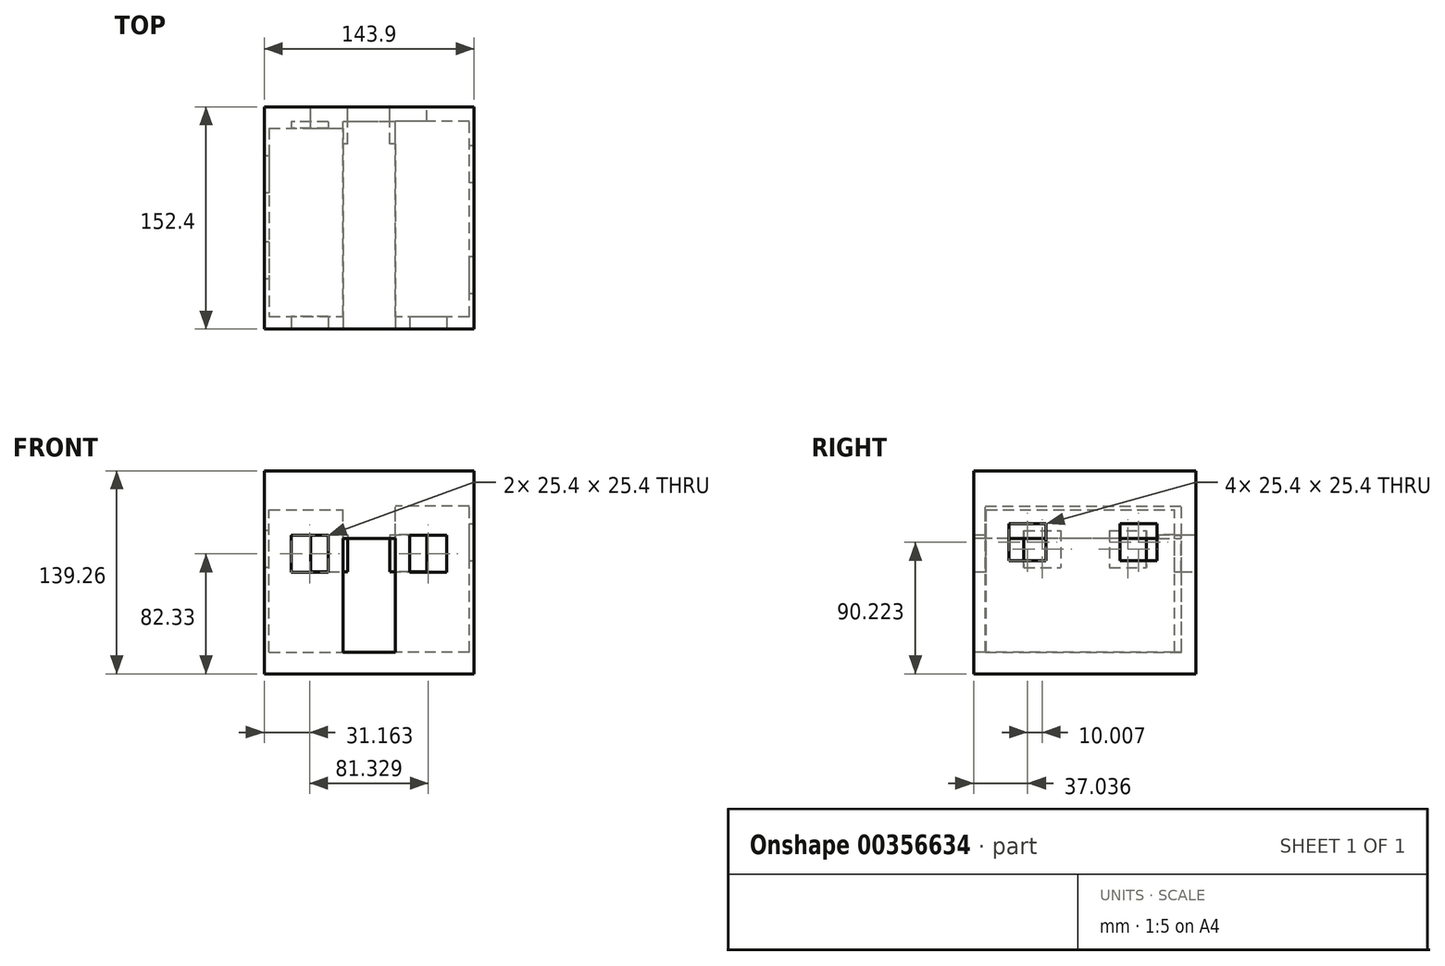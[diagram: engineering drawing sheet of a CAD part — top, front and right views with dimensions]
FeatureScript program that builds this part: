
annotation { "Feature Type Name" : "Feature", "Feature Type Description" : "" }
export const myFeature = defineFeature(function(context is Context, id is Id, definition is map)
    precondition{}
    {
        {
            var Q0;
            Q0=qCreatedBy(makeId("Front.planeOp"),FACE);
            var sketch = newSketch(context, id + "F0", { "sketchPlane" : qUnion([Q0])});
            skLineSegment(sketch, "E0.bottom", {"start": v(71.95, 69.63) * mm, "end": v(-71.95, 69.63) * mm});
            skLineSegment(sketch, "E0.top", {"start": v(71.95, -69.63) * mm, "end": v(-71.95, -69.63) * mm});
            skLineSegment(sketch, "E0.left", {"start": v(71.95, 69.63) * mm, "end": v(71.95, -69.63) * mm});
            skLineSegment(sketch, "E0.right", {"start": v(-71.95, 69.63) * mm, "end": v(-71.95, -69.63) * mm});
            skPoint(sketch, "E0.middle", {"position": v(0, 0) * mm});
            skSolve(sketch);
        }
        {
            var Q0;
            Q0=makeQuery(id+"F0.imprint","IMPRINT",FACE,{"disambiguationData":[TD([[makeQuery(id+"F0.imprint","IMPRINT",EDGE,{"derivedFrom":sQuery(id+"F0.wireOp",EDGE,"E0.bottom")}),1.0]])]});
            extrude(context, id + "F1", {"entities" : qUnion([Q0]), "depth" : 152.4 * mm});
        }
        {
            var Q0;
            Q0=makeQuery(id+"F1.opExtrude","CAP_FACE",FACE,{"disambiguationData":[OSD([sQuery(id+"F0.wireOp",EDGE,"E0.bottom"),sQuery(id+"F0.wireOp",EDGE,"E0.top"),sQuery(id+"F0.wireOp",EDGE,"E0.left"),sQuery(id+"F0.wireOp",EDGE,"E0.right")])],"isStart":false});
            var sketch = newSketch(context, id + "F2", { "sketchPlane" : qUnion([Q0])});
            skLineSegment(sketch, "E1.bottom", {"start": v(17.83, 23.45) * mm, "end": v(-17.83, 23.45) * mm});
            skLineSegment(sketch, "E1.top", {"start": v(17.83, -54.7) * mm, "end": v(-17.83, -54.7) * mm});
            skLineSegment(sketch, "E1.left", {"start": v(17.83, 23.45) * mm, "end": v(17.83, -54.7) * mm});
            skLineSegment(sketch, "E1.right", {"start": v(-17.83, 23.45) * mm, "end": v(-17.83, -54.7) * mm});
            skPoint(sketch, "E1.middle", {"position": v(0, -15.63) * mm});
            skLineSegment(sketch, "E2.bottom", {"start": v(-28.09, 0) * mm, "end": v(-53.49, 0) * mm});
            skLineSegment(sketch, "E2.top", {"start": v(-28.09, 25.4) * mm, "end": v(-53.49, 25.4) * mm});
            skLineSegment(sketch, "E2.left", {"start": v(-28.09, 0) * mm, "end": v(-28.09, 25.4) * mm});
            skLineSegment(sketch, "E2.right", {"start": v(-53.49, 0) * mm, "end": v(-53.49, 25.4) * mm});
            skPoint(sketch, "E2.middle", {"position": v(-40.79, 12.7) * mm});
            skLineSegment(sketch, "E3.bottom", {"start": v(27.84, 0) * mm, "end": v(53.24, 0) * mm});
            skLineSegment(sketch, "E3.top", {"start": v(27.84, 25.4) * mm, "end": v(53.24, 25.4) * mm});
            skLineSegment(sketch, "E3.left", {"start": v(27.84, 0) * mm, "end": v(27.84, 25.4) * mm});
            skLineSegment(sketch, "E3.right", {"start": v(53.24, 0) * mm, "end": v(53.24, 25.4) * mm});
            skPoint(sketch, "E3.middle", {"position": v(40.54, 12.7) * mm});
            skSolve(sketch);
        }
        {
            var Q0;
            Q0=makeQuery(id+"F2.imprint","IMPRINT",FACE,{"disambiguationData":[TD([[makeQuery(id+"F2.imprint","IMPRINT",EDGE,{"derivedFrom":sQuery(id+"F2.wireOp",EDGE,"E2.bottom")}),-1.0]])]});
            var Q1;
            Q1=makeQuery(id+"F2.imprint","IMPRINT",FACE,{"disambiguationData":[TD([[makeQuery(id+"F2.imprint","IMPRINT",EDGE,{"derivedFrom":sQuery(id+"F2.wireOp",EDGE,"E3.bottom")}),1.0]])]});
            var Q2;
            Q2=makeQuery(id+"F2.imprint","IMPRINT",FACE,{"disambiguationData":[TD([[makeQuery(id+"F2.imprint","IMPRINT",EDGE,{"derivedFrom":sQuery(id+"F2.wireOp",EDGE,"E1.bottom")}),1.0]])]});
            extrude(context, id + "F3", {"entities" : qUnion([Q0, Q1, Q2]), "operationType" : NewBodyOperationType.REMOVE, "oppositeDirection" : true, "depth" : 142.24 * mm});
        }
        {
            var Q0;
            Q0=makeQuery(id+"F3.boolean.opBoolean","COPY",FACE,{"derivedFrom":makeQuery(id+"F3.opExtrude","SWEPT_FACE",FACE,{"disambiguationData":[OSD([sQuery(id+"F2.wireOp",EDGE,"E1.right")])]})});
            var sketch = newSketch(context, id + "F4", { "sketchPlane" : qUnion([Q0])});
            skLineSegment(sketch, "E4.bottom", {"start": v(-143.72, -46.42) * mm, "end": v(-14.63, -46.42) * mm});
            skLineSegment(sketch, "E4.top", {"start": v(-143.72, 42.99) * mm, "end": v(-14.63, 42.99) * mm});
            skLineSegment(sketch, "E4.left", {"start": v(-143.72, -46.42) * mm, "end": v(-143.72, 42.99) * mm});
            skLineSegment(sketch, "E4.right", {"start": v(-14.63, -46.42) * mm, "end": v(-14.63, 42.99) * mm});
            skSolve(sketch);
        }
        {
            var Q0;
            Q0 = qSketchRegion(id + "F4", true);
            extrude(context, id + "F5", {"entities" : qUnion([Q0]), "operationType" : NewBodyOperationType.REMOVE, "oppositeDirection" : true, "depth" : 50.8 * mm});
        }
        {
            var Q0;
            Q0=makeQuery(id+"F3.boolean.opBoolean","COPY",FACE,{"derivedFrom":makeQuery(id+"F3.opExtrude","SWEPT_FACE",FACE,{"disambiguationData":[OSD([sQuery(id+"F2.wireOp",EDGE,"E1.left")])]})});
            var sketch = newSketch(context, id + "F6", { "sketchPlane" : qUnion([Q0])});
            skLineSegment(sketch, "E5.bottom", {"start": v(144.24, -54.7) * mm, "end": v(9.85, -54.7) * mm});
            skLineSegment(sketch, "E5.top", {"start": v(144.24, 45.49) * mm, "end": v(9.85, 45.49) * mm});
            skLineSegment(sketch, "E5.left", {"start": v(144.24, -54.7) * mm, "end": v(144.24, 45.49) * mm});
            skLineSegment(sketch, "E5.right", {"start": v(9.85, -54.7) * mm, "end": v(9.85, 45.49) * mm});
            skSolve(sketch);
        }
        {
            var Q0;
            Q0 = qSketchRegion(id + "F6", true);
            extrude(context, id + "F7", {"entities" : qUnion([Q0]), "operationType" : NewBodyOperationType.REMOVE, "oppositeDirection" : true, "depth" : 50.8 * mm});
        }
        {
            var Q0;
            Q0=makeQuery(id+"F3.boolean.opBoolean","COPY",FACE,{"derivedFrom":makeQuery(id+"F3.opExtrude","SWEPT_FACE",FACE,{"disambiguationData":[OSD([sQuery(id+"F2.wireOp",EDGE,"E1.right")])]})});
            var sketch = newSketch(context, id + "F8", { "sketchPlane" : qUnion([Q0])});
            skLineSegment(sketch, "E6.bottom", {"start": v(-143.72, -46.42) * mm, "end": v(-14.63, -46.42) * mm});
            skLineSegment(sketch, "E6.top", {"start": v(-143.72, -54.7) * mm, "end": v(-14.63, -54.7) * mm});
            skLineSegment(sketch, "E6.left", {"start": v(-143.72, -46.42) * mm, "end": v(-143.72, -54.7) * mm});
            skLineSegment(sketch, "E6.right", {"start": v(-14.63, -46.42) * mm, "end": v(-14.63, -54.7) * mm});
            skSolve(sketch);
        }
        {
            var Q0;
            Q0 = qSketchRegion(id + "F8", true);
            extrude(context, id + "F9", {"entities" : qUnion([Q0]), "operationType" : NewBodyOperationType.REMOVE, "oppositeDirection" : true, "depth" : 50.8 * mm});
        }
        {
            var Q0;
            Q0=makeQuery(id+"F1.opExtrude","SWEPT_FACE",FACE,{"disambiguationData":[OSD([sQuery(id+"F0.wireOp",EDGE,"E0.left")])]});
            var sketch = newSketch(context, id + "F10", { "sketchPlane" : qUnion([Q0])});
            skLineSegment(sketch, "E7.bottom", {"start": v(-102.66, 33.3) * mm, "end": v(-128.06, 33.3) * mm});
            skLineSegment(sketch, "E7.top", {"start": v(-102.66, 7.9) * mm, "end": v(-128.06, 7.9) * mm});
            skLineSegment(sketch, "E7.left", {"start": v(-102.66, 33.3) * mm, "end": v(-102.66, 7.9) * mm});
            skLineSegment(sketch, "E7.right", {"start": v(-128.06, 33.3) * mm, "end": v(-128.06, 7.9) * mm});
            skPoint(sketch, "E7.middle", {"position": v(-115.36, 20.6) * mm});
            skLineSegment(sketch, "E8.bottom", {"start": v(-26.46, 33.3) * mm, "end": v(-51.86, 33.3) * mm});
            skLineSegment(sketch, "E8.top", {"start": v(-26.46, 7.9) * mm, "end": v(-51.86, 7.9) * mm});
            skLineSegment(sketch, "E8.left", {"start": v(-26.46, 33.3) * mm, "end": v(-26.46, 7.9) * mm});
            skLineSegment(sketch, "E8.right", {"start": v(-51.86, 33.3) * mm, "end": v(-51.86, 7.9) * mm});
            skPoint(sketch, "E8.middle", {"position": v(-39.16, 20.6) * mm});
            skSolve(sketch);
        }
        {
            var Q0;
            Q0=makeQuery(id+"F10.imprint","IMPRINT",FACE,{"disambiguationData":[TD([[makeQuery(id+"F10.imprint","IMPRINT",EDGE,{"derivedFrom":sQuery(id+"F10.wireOp",EDGE,"E7.bottom")}),1.0]])]});
            var Q1;
            Q1=makeQuery(id+"F10.imprint","IMPRINT",FACE,{"disambiguationData":[TD([[makeQuery(id+"F10.imprint","IMPRINT",EDGE,{"derivedFrom":sQuery(id+"F10.wireOp",EDGE,"E8.bottom")}),1.0]])]});
            extrude(context, id + "F11", {"entities" : qUnion([Q0, Q1]), "operationType" : NewBodyOperationType.REMOVE, "oppositeDirection" : true, "depth" : 25.4 * mm});
        }
        {
            var Q0;
            Q0=makeQuery(id+"F1.opExtrude","SWEPT_FACE",FACE,{"disambiguationData":[OSD([sQuery(id+"F0.wireOp",EDGE,"E0.right")])]});
            var sketch = newSketch(context, id + "F12", { "sketchPlane" : qUnion([Q0])});
            skLineSegment(sketch, "E9.bottom", {"start": v(59.18, 28.78) * mm, "end": v(33.78, 28.78) * mm});
            skLineSegment(sketch, "E9.top", {"start": v(59.18, 3.38) * mm, "end": v(33.78, 3.38) * mm});
            skLineSegment(sketch, "E9.left", {"start": v(59.18, 28.78) * mm, "end": v(59.18, 3.38) * mm});
            skLineSegment(sketch, "E9.right", {"start": v(33.78, 28.78) * mm, "end": v(33.78, 3.38) * mm});
            skPoint(sketch, "E9.middle", {"position": v(46.48, 16.08) * mm});
            skLineSegment(sketch, "E10.bottom", {"start": v(118.06, 28.78) * mm, "end": v(92.66, 28.78) * mm});
            skLineSegment(sketch, "E10.top", {"start": v(118.06, 3.38) * mm, "end": v(92.66, 3.38) * mm});
            skLineSegment(sketch, "E10.left", {"start": v(118.06, 28.78) * mm, "end": v(118.06, 3.38) * mm});
            skLineSegment(sketch, "E10.right", {"start": v(92.66, 28.78) * mm, "end": v(92.66, 3.38) * mm});
            skPoint(sketch, "E10.middle", {"position": v(105.36, 16.08) * mm});
            skSolve(sketch);
        }
        {
            var Q0;
            Q0=makeQuery(id+"F12.imprint","IMPRINT",FACE,{"disambiguationData":[TD([[makeQuery(id+"F12.imprint","IMPRINT",EDGE,{"derivedFrom":sQuery(id+"F12.wireOp",EDGE,"E9.bottom")}),1.0]])]});
            var Q1;
            Q1=makeQuery(id+"F12.imprint","IMPRINT",FACE,{"disambiguationData":[TD([[makeQuery(id+"F12.imprint","IMPRINT",EDGE,{"derivedFrom":sQuery(id+"F12.wireOp",EDGE,"E10.bottom")}),1.0]])]});
            extrude(context, id + "F13", {"entities" : qUnion([Q0, Q1]), "operationType" : NewBodyOperationType.REMOVE, "oppositeDirection" : true, "depth" : 50.8 * mm});
        }
        {
            var Q0;
            Q0=makeQuery(id+"F1.opExtrude","CAP_FACE",FACE,{"disambiguationData":[OSD([sQuery(id+"F0.wireOp",EDGE,"E0.bottom"),sQuery(id+"F0.wireOp",EDGE,"E0.top"),sQuery(id+"F0.wireOp",EDGE,"E0.left"),sQuery(id+"F0.wireOp",EDGE,"E0.right")])],"isStart":true});
            var sketch = newSketch(context, id + "F14", { "sketchPlane" : qUnion([Q0])});
            skLineSegment(sketch, "E11.bottom", {"start": v(-14.2, 25.9) * mm, "end": v(-39.6, 25.9) * mm});
            skLineSegment(sketch, "E11.top", {"start": v(-14.2, 0.5) * mm, "end": v(-39.6, 0.5) * mm});
            skLineSegment(sketch, "E11.left", {"start": v(-14.2, 25.9) * mm, "end": v(-14.2, 0.5) * mm});
            skLineSegment(sketch, "E11.right", {"start": v(-39.6, 25.9) * mm, "end": v(-39.6, 0.5) * mm});
            skPoint(sketch, "E11.middle", {"position": v(-26.9, 13.2) * mm});
            skLineSegment(sketch, "E12.bottom", {"start": v(40.08, 25.9) * mm, "end": v(14.68, 25.9) * mm});
            skLineSegment(sketch, "E12.top", {"start": v(40.08, 0.5) * mm, "end": v(14.68, 0.5) * mm});
            skLineSegment(sketch, "E12.left", {"start": v(40.08, 25.9) * mm, "end": v(40.08, 0.5) * mm});
            skLineSegment(sketch, "E12.right", {"start": v(14.68, 25.9) * mm, "end": v(14.68, 0.5) * mm});
            skPoint(sketch, "E12.middle", {"position": v(27.38, 13.2) * mm});
            skSolve(sketch);
        }
        {
            var Q0;
            Q0=makeQuery(id+"F14.imprint","IMPRINT",FACE,{"disambiguationData":[TD([[makeQuery(id+"F14.imprint","IMPRINT",EDGE,{"derivedFrom":sQuery(id+"F14.wireOp",EDGE,"E11.bottom")}),1.0]])]});
            var Q1;
            Q1=makeQuery(id+"F14.imprint","IMPRINT",FACE,{"disambiguationData":[TD([[makeQuery(id+"F14.imprint","IMPRINT",EDGE,{"derivedFrom":sQuery(id+"F14.wireOp",EDGE,"E12.bottom")}),1.0]])]});
            extrude(context, id + "F15", {"entities" : qUnion([Q0, Q1]), "operationType" : NewBodyOperationType.REMOVE, "oppositeDirection" : true, "depth" : 25.4 * mm});
        }
    });
